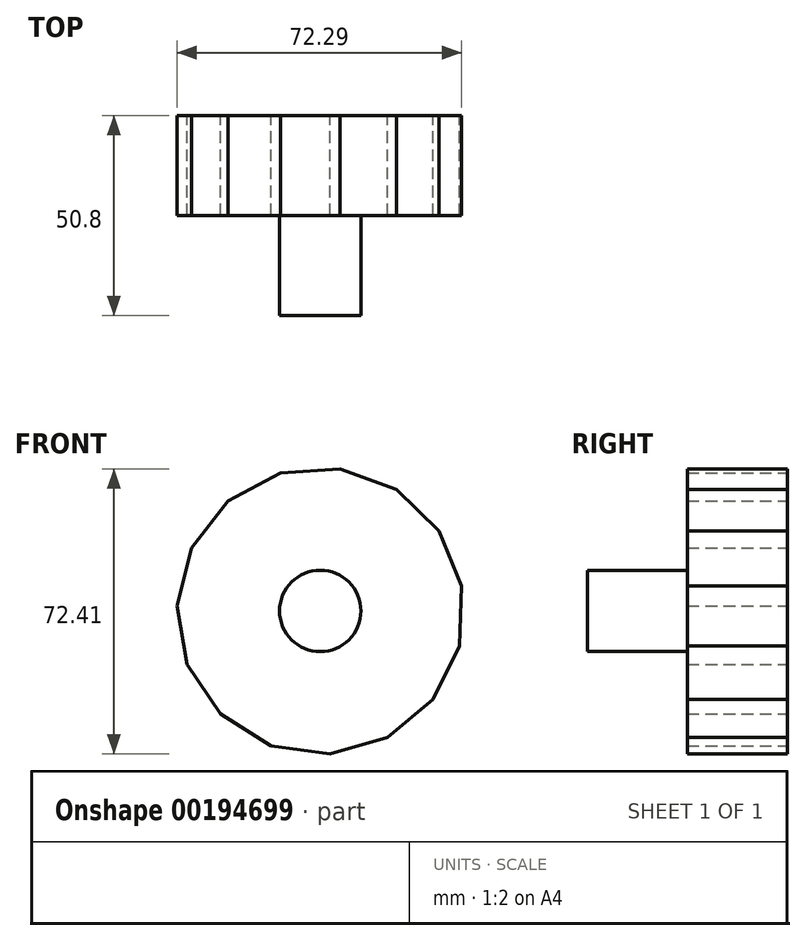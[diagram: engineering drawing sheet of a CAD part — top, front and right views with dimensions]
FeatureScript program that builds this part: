
annotation { "Feature Type Name" : "Feature", "Feature Type Description" : "" }
export const myFeature = defineFeature(function(context is Context, id is Id, definition is map)
    precondition{}
    {
        {
            var Q0;
            Q0=qCreatedBy(makeId("Front.planeOp"),FACE);
            var sketch = newSketch(context, id + "F0", { "sketchPlane" : qUnion([Q0])});
            skCircle(sketch, "E0.cCircle", {"center": v(0, 0) * mm, "radius": 35.64 * mm, "construction": true});
            skLineSegment(sketch, "E0.0", {"start": v(5.1, 36.07) * mm, "end": v(19.33, 30.88) * mm});
            skLineSegment(sketch, "E0.1", {"start": v(19.33, 30.88) * mm, "end": v(30.22, 20.35) * mm});
            skLineSegment(sketch, "E0.2", {"start": v(30.22, 20.35) * mm, "end": v(35.88, 6.3) * mm});
            skLineSegment(sketch, "E0.3", {"start": v(35.88, 6.3) * mm, "end": v(35.34, -8.84) * mm});
            skLineSegment(sketch, "E0.4", {"start": v(35.34, -8.84) * mm, "end": v(28.7, -22.45) * mm});
            skLineSegment(sketch, "E0.5", {"start": v(28.7, -22.45) * mm, "end": v(17.08, -32.18) * mm});
            skLineSegment(sketch, "E0.6", {"start": v(17.08, -32.18) * mm, "end": v(2.52, -36.34) * mm});
            skLineSegment(sketch, "E0.7", {"start": v(2.52, -36.34) * mm, "end": v(-12.48, -34.23) * mm});
            skLineSegment(sketch, "E0.8", {"start": v(-12.48, -34.23) * mm, "end": v(-25.33, -26.19) * mm});
            skLineSegment(sketch, "E0.9", {"start": v(-25.33, -26.19) * mm, "end": v(-33.79, -13.62) * mm});
            skLineSegment(sketch, "E0.10", {"start": v(-33.79, -13.62) * mm, "end": v(-36.4, 1.3) * mm});
            skLineSegment(sketch, "E0.11", {"start": v(-36.4, 1.3) * mm, "end": v(-32.73, 16) * mm});
            skLineSegment(sketch, "E0.12", {"start": v(-32.73, 16) * mm, "end": v(-23.4, 27.93) * mm});
            skLineSegment(sketch, "E0.13", {"start": v(-23.4, 27.93) * mm, "end": v(-10.02, 35.03) * mm});
            skLineSegment(sketch, "E0.14", {"start": v(-10.02, 35.03) * mm, "end": v(5.1, 36.07) * mm});
            skPoint(sketch, "E0.0.midPoint", {"position": v(12.21, 33.48) * mm});
            skSolve(sketch);
        }
        {
            var Q0;
            Q0=makeQuery(id+"F0.imprint","IMPRINT",FACE,{"disambiguationData":[TD([[makeQuery(id+"F0.imprint","IMPRINT",EDGE,{"derivedFrom":sQuery(id+"F0.wireOp",EDGE,"E0.0")}),-1.0]])]});
            extrude(context, id + "F1", {"entities" : qUnion([Q0]), "depth" : 25.4 * mm});
        }
        {
            var Q0;
            Q0=makeQuery(id+"F1.opExtrude","CAP_FACE",FACE,{"disambiguationData":[OSD([sQuery(id+"F0.wireOp",EDGE,"E0.0"),sQuery(id+"F0.wireOp",EDGE,"E0.1"),sQuery(id+"F0.wireOp",EDGE,"E0.2"),sQuery(id+"F0.wireOp",EDGE,"E0.3"),sQuery(id+"F0.wireOp",EDGE,"E0.4"),sQuery(id+"F0.wireOp",EDGE,"E0.5"),sQuery(id+"F0.wireOp",EDGE,"E0.6"),sQuery(id+"F0.wireOp",EDGE,"E0.7"),sQuery(id+"F0.wireOp",EDGE,"E0.8"),sQuery(id+"F0.wireOp",EDGE,"E0.9"),sQuery(id+"F0.wireOp",EDGE,"E0.10"),sQuery(id+"F0.wireOp",EDGE,"E0.11"),sQuery(id+"F0.wireOp",EDGE,"E0.12"),sQuery(id+"F0.wireOp",EDGE,"E0.13"),sQuery(id+"F0.wireOp",EDGE,"E0.14")])],"isStart":false});
            var sketch = newSketch(context, id + "F2", { "sketchPlane" : qUnion([Q0])});
            skCircle(sketch, "E1", {"center": v(0, 0) * mm, "radius": 10.34 * mm});
            skSolve(sketch);
        }
        {
            var Q0;
            Q0=makeQuery(id+"F2.imprint","IMPRINT",FACE,{"disambiguationData":[TD([[makeQuery(id+"F2.imprint","IMPRINT",EDGE,{"derivedFrom":sQuery(id+"F2.wireOp",EDGE,"E1")}),1.0]])]});
            extrude(context, id + "F3", {"entities" : qUnion([Q0]), "operationType" : NewBodyOperationType.ADD, "depth" : 25.4 * mm});
        }
    });
